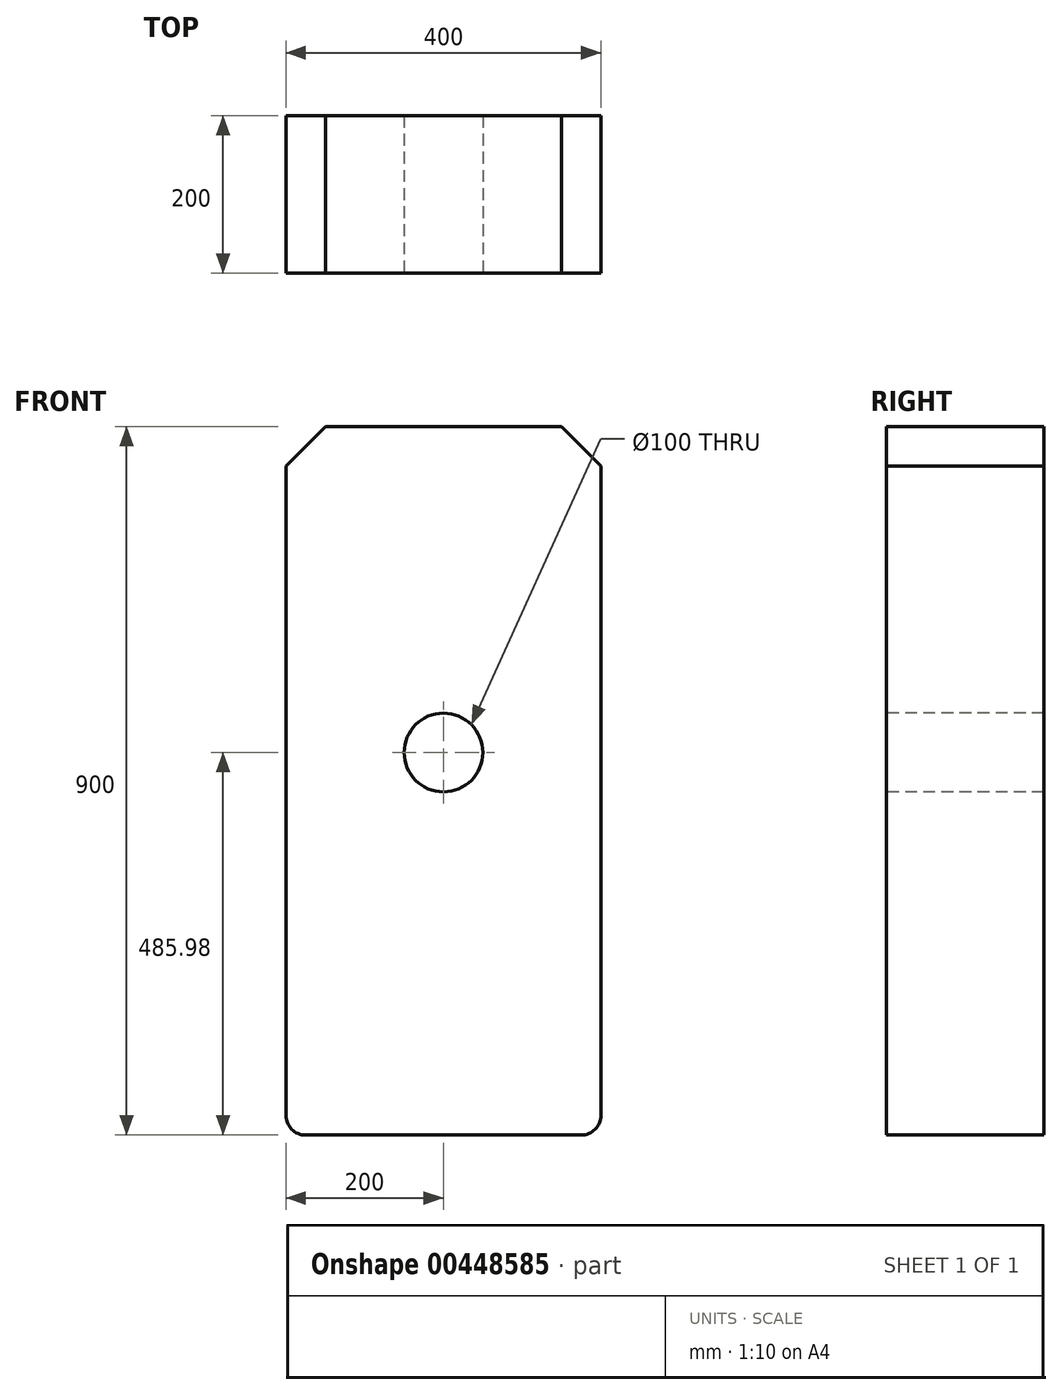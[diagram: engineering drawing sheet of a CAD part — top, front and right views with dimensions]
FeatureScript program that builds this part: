
annotation { "Feature Type Name" : "Feature", "Feature Type Description" : "" }
export const myFeature = defineFeature(function(context is Context, id is Id, definition is map)
    precondition{}
    {
        {
            var Q0;
            Q0=qCreatedBy(makeId("Front.planeOp"),FACE);
            var sketch = newSketch(context, id + "F0", { "sketchPlane" : qUnion([Q0])});
            skLineSegment(sketch, "E0.bottom", {"start": v(200, 414.02) * mm, "end": v(-200, 414.02) * mm});
            skLineSegment(sketch, "E0.top", {"start": v(200, -485.98) * mm, "end": v(-200, -485.98) * mm});
            skLineSegment(sketch, "E0.left", {"start": v(200, 414.02) * mm, "end": v(200, -485.98) * mm});
            skLineSegment(sketch, "E0.right", {"start": v(-200, 414.02) * mm, "end": v(-200, -485.98) * mm});
            skPoint(sketch, "E0.middle", {"position": v(0, -35.98) * mm});
            skSolve(sketch);
        }
        {
            var Q0;
            Q0 = qSketchRegion(id + "F0", true);
            extrude(context, id + "F1", {"entities" : qUnion([Q0]), "depth" : 200 * mm});
        }
        {
            var Q0;
            Q0=makeQuery(id+"F1.opExtrude","SWEPT_EDGE",EDGE,{"disambiguationData":[OSD([sQuery(id+"F0.wireOp",EDGE,"E0.bottom"),sQuery(id+"F0.wireOp",EDGE,"E0.right")])]});
            var Q1;
            Q1=makeQuery(id+"F1.opExtrude","SWEPT_EDGE",EDGE,{"disambiguationData":[OSD([sQuery(id+"F0.wireOp",EDGE,"E0.bottom"),sQuery(id+"F0.wireOp",EDGE,"E0.left")])]});
            chamfer(context, id + "F2", {"entities" : qUnion([Q0, Q1]), "width" : 50 * mm, "tangentPropagation" : true});
        }
        {
            var Q0;
            Q0=makeQuery(id+"F1.opExtrude","SWEPT_EDGE",EDGE,{"disambiguationData":[OSD([sQuery(id+"F0.wireOp",EDGE,"E0.top"),sQuery(id+"F0.wireOp",EDGE,"E0.right")])]});
            var Q1;
            Q1=makeQuery(id+"F1.opExtrude","SWEPT_EDGE",EDGE,{"disambiguationData":[OSD([sQuery(id+"F0.wireOp",EDGE,"E0.top"),sQuery(id+"F0.wireOp",EDGE,"E0.left")])]});
            fillet(context, id + "F3", {"entities" : qUnion([Q0, Q1]), "radius" : 25 * mm, "tangentPropagation" : true, "allowEdgeOverflow" : false});
        }
        {
            var Q0;
            Q0=makeQuery(id+"F1.opExtrude","CAP_FACE",FACE,{"disambiguationData":[OSD([sQuery(id+"F0.wireOp",EDGE,"E0.bottom"),sQuery(id+"F0.wireOp",EDGE,"E0.top"),sQuery(id+"F0.wireOp",EDGE,"E0.left"),sQuery(id+"F0.wireOp",EDGE,"E0.right")])],"isStart":false});
            var sketch = newSketch(context, id + "F4", { "sketchPlane" : qUnion([Q0])});
            skCircle(sketch, "E1", {"center": v(0, 0) * mm, "radius": 50 * mm});
            skSolve(sketch);
        }
        {
            var Q0;
            Q0 = qSketchRegion(id + "F4", true);
            extrude(context, id + "F5", {"entities" : qUnion([Q0]), "operationType" : NewBodyOperationType.REMOVE, "endBound" : BoundingType.THROUGH_ALL, "oppositeDirection" : true, "depth" : 25.4 * mm});
        }
    });
